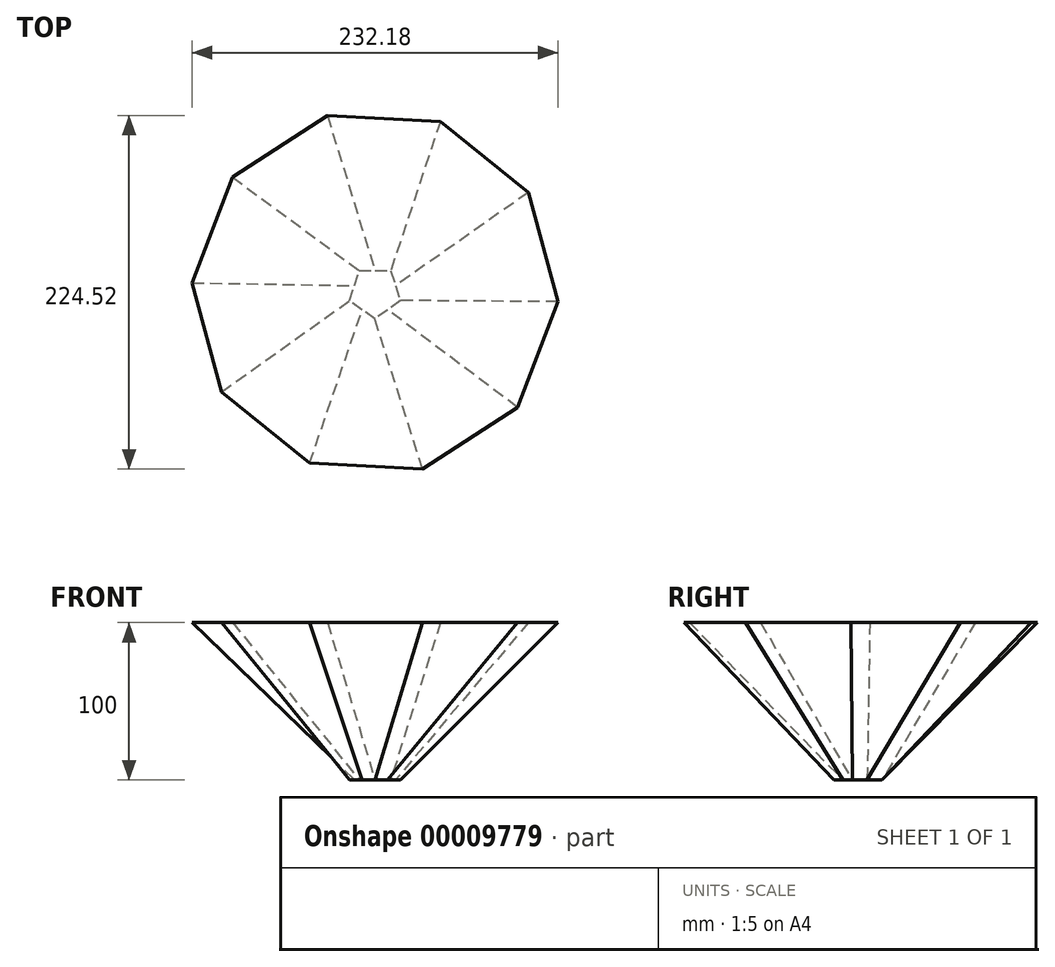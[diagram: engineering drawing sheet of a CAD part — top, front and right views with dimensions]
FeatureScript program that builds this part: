
annotation { "Feature Type Name" : "Feature", "Feature Type Description" : "" }
export const myFeature = defineFeature(function(context is Context, id is Id, definition is map)
    precondition{}
    {
        {
            var Q0;
            Q0=qCreatedBy(makeId("Top.planeOp"),FACE);
            var sketch = newSketch(context, id + "F0", { "sketchPlane" : qUnion([Q0])});
            skCircle(sketch, "E0.cCircle", {"center": v(0, 0) * mm, "radius": 13.76 * mm, "construction": true});
            skLineSegment(sketch, "E0.0", {"start": v(10, 13.76) * mm, "end": v(16.18, -5.26) * mm});
            skLineSegment(sketch, "E0.1", {"start": v(16.18, -5.26) * mm, "end": v(0, -17.01) * mm});
            skLineSegment(sketch, "E0.2", {"start": v(0, -17.01) * mm, "end": v(-16.18, -5.26) * mm});
            skLineSegment(sketch, "E0.3", {"start": v(-16.18, -5.26) * mm, "end": v(-10, 13.76) * mm});
            skLineSegment(sketch, "E0.4", {"start": v(-10, 13.76) * mm, "end": v(10, 13.76) * mm});
            skPoint(sketch, "E0.0.midPoint", {"position": v(13.1, 4.25) * mm});
            skLineSegment(sketch, "E1", {"start": v(0, -17.01) * mm, "end": v(0, 0) * mm, "construction": true});
            skLineSegment(sketch, "E2", {"start": v(0, 0) * mm, "end": v(10, 13.76) * mm, "construction": true});
            skLineSegment(sketch, "E3", {"start": v(0, 0) * mm, "end": v(16.18, -5.26) * mm, "construction": true});
            skLineSegment(sketch, "E4", {"start": v(0, 0) * mm, "end": v(-16.18, -5.26) * mm, "construction": true});
            skLineSegment(sketch, "E5", {"start": v(0, 0) * mm, "end": v(-10, 13.76) * mm, "construction": true});
            skSolve(sketch);
        }
        {
            var Q0;
            Q0=qCreatedBy(makeId("Top.planeOp"),FACE);
            cPlane(context, id + "F1", {"entities" : qUnion([Q0]), "cplaneType" : CPlaneType.OFFSET, "offset" : 100 * mm, "width" : 150 * mm, "height" : 150 * mm});
        }
        {
            var Q0;
            Q0=qCreatedBy(id+"F1.planeOp",FACE);
            var sketch = newSketch(context, id + "F2", { "sketchPlane" : qUnion([Q0])});
            skCircle(sketch, "E6.cCircle", {"center": v(0, 0) * mm, "radius": 110.56 * mm, "construction": true});
            skLineSegment(sketch, "E6.0", {"start": v(97.43, 63.4) * mm, "end": v(116.1, -5.97) * mm});
            skLineSegment(sketch, "E6.1", {"start": v(116.1, -5.97) * mm, "end": v(90.41, -73.07) * mm});
            skLineSegment(sketch, "E6.2", {"start": v(90.41, -73.07) * mm, "end": v(30.2, -112.26) * mm});
            skLineSegment(sketch, "E6.3", {"start": v(30.2, -112.26) * mm, "end": v(-41.55, -108.57) * mm});
            skLineSegment(sketch, "E6.4", {"start": v(-41.55, -108.57) * mm, "end": v(-97.43, -63.4) * mm});
            skLineSegment(sketch, "E6.5", {"start": v(-97.43, -63.4) * mm, "end": v(-116.1, 5.97) * mm});
            skLineSegment(sketch, "E6.6", {"start": v(-116.1, 5.97) * mm, "end": v(-90.41, 73.07) * mm});
            skLineSegment(sketch, "E6.7", {"start": v(-90.41, 73.07) * mm, "end": v(-30.2, 112.26) * mm});
            skLineSegment(sketch, "E6.8", {"start": v(-30.2, 112.26) * mm, "end": v(41.55, 108.57) * mm});
            skLineSegment(sketch, "E6.9", {"start": v(41.55, 108.57) * mm, "end": v(97.43, 63.4) * mm});
            skPoint(sketch, "E6.0.midPoint", {"position": v(106.76, 28.72) * mm});
            skSolve(sketch);
        }
        {
            var Q0;
            Q0=makeQuery(id+"F2.imprint","IMPRINT",FACE,{"disambiguationData":[TD([[makeQuery(id+"F2.imprint","IMPRINT",EDGE,{"derivedFrom":sQuery(id+"F2.wireOp",EDGE,"E6.0")}),-1.0]])]});
            var Q1;
            Q1=makeQuery(id+"F0.imprint","IMPRINT",FACE,{"disambiguationData":[TD([[makeQuery(id+"F0.imprint","IMPRINT",EDGE,{"derivedFrom":sQuery(id+"F0.wireOp",EDGE,"E0.0")}),-1.0]])]});
            var Q2;
            Q2=sQuery(id+"F2.wireOp",VERTEX,"E6.9.start");
            var Q3;
            Q3=sQuery(id+"F0.wireOp",VERTEX,"E0.0.start");
            loft(context, id + "F3", {"sheetProfilesArray" : [{ "sheetProfileEntities" : qUnion([Q0]) }, { "sheetProfileEntities" : qUnion([Q1]) }], "matchConnections" : true, "connections" : [{ "connectionEntities" : qUnion([Q2, Q3]), "connectionEdgeQueries" : qUnion([]), "connectionEdgeParameters" : [] }]});
        }
    });
